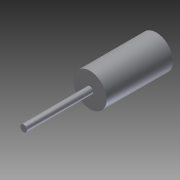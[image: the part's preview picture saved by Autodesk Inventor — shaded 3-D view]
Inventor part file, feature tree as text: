
AUTODESK INVENTOR PART (.ipt)
format: ipt  version: 2012 (Build 160160000, 160)  size: 77,824 bytes
history: native  units: in
note: dims shown in document units (in); Inventor stores cm internally (conversion verified against a paired STEP export)
features: extrude x2, sketch x2
ambient origin geometry x8: Origin, YZ Plane, XZ Plane, XY Plane, X Axis, Y Axis, Z Axis, Center Point
bodies: Solid1 (feature_tree)
feature tree (4):
  extrude  "Extrusion1"  Depth=10.0in TaperAngle=0.0deg
  extrude  "Extrusion2"  Depth=10.0in TaperAngle=0.0deg
  sketch  "Sketch1"  dims[d0=5.0in d1=10.0in d2=0.0in]
  sketch  "Sketch2"  dims[d3=1.0in d4=10.0in d5=0.0in]
